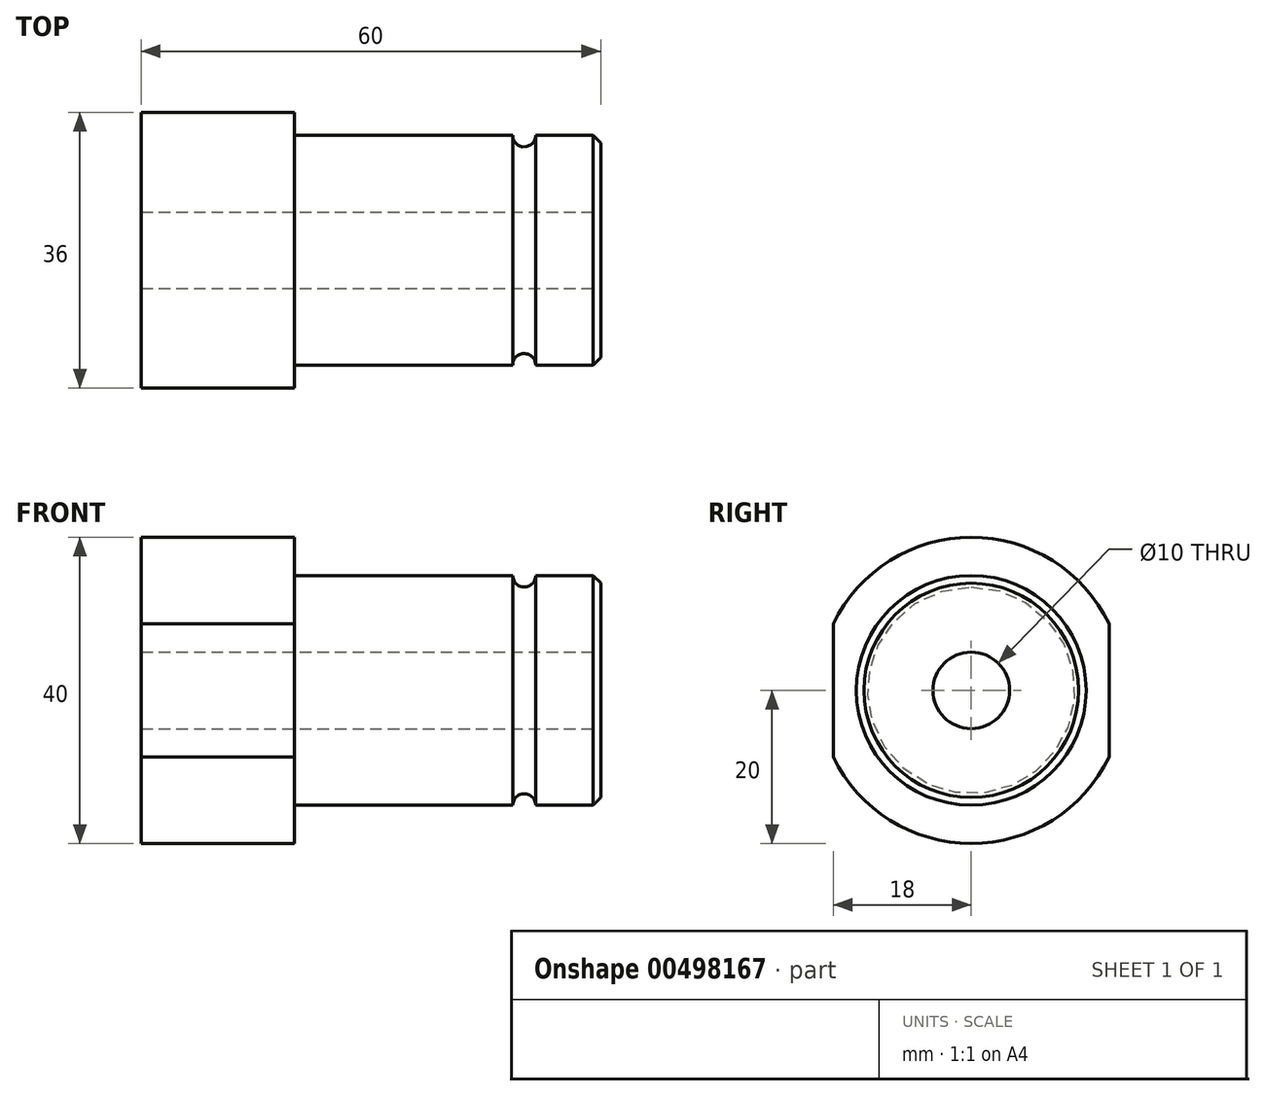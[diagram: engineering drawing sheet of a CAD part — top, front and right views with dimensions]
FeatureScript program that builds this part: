
annotation { "Feature Type Name" : "Feature", "Feature Type Description" : "" }
export const myFeature = defineFeature(function(context is Context, id is Id, definition is map)
    precondition{}
    {
        {
            var Q0;
            Q0=qCreatedBy(makeId("Front.planeOp"),FACE);
            var sketch = newSketch(context, id + "F0", { "sketchPlane" : qUnion([Q0])});
            skLineSegment(sketch, "E0", {"start": v(0, 0) * mm, "end": v(0, 20) * mm});
            skLineSegment(sketch, "E1", {"start": v(0, 20) * mm, "end": v(20, 20) * mm});
            skLineSegment(sketch, "E2", {"start": v(20, 20) * mm, "end": v(20, 15) * mm});
            skLineSegment(sketch, "E3", {"start": v(20, 15) * mm, "end": v(60, 15) * mm});
            skLineSegment(sketch, "E4", {"start": v(60, 15) * mm, "end": v(60, 0) * mm});
            skLineSegment(sketch, "E5", {"start": v(60, 0) * mm, "end": v(0, 0) * mm});
            skLineSegment(sketch, "E6", {"start": v(-6.51, 0) * mm, "end": v(42.86, 0) * mm, "construction": true});
            skCircle(sketch, "E7", {"center": v(50, 15) * mm, "radius": 1.5 * mm});
            skSolve(sketch);
        }
        {
            var Q0;
            Q0=makeQuery(id+"F0.imprint","IMPRINT",FACE,{"disambiguationData":[TD([[makeQuery(id+"F0.imprint","IMPRINT",EDGE,{"derivedFrom":sQuery(id+"F0.wireOp",EDGE,"E0")}),-1.0]])]});
            var Q1;
            Q1=sQuery(id+"F0.wireOp",EDGE,"E6");
            revolve(context, id + "F1", {"entities" : qUnion([Q0]), "axis" : qUnion([Q1]), "revolveType" : RevolveType.FULL});
        }
        {
            var Q0;
            Q0=makeQuery(id+"F1.opRevolve","SWEPT_EDGE",EDGE,{"disambiguationData":[OSD([sQuery(id+"F0.wireOp",EDGE,"E3"),sQuery(id+"F0.wireOp",EDGE,"E4")])]});
            chamfer(context, id + "F2", {"entities" : qUnion([Q0]), "width" : 1 * mm, "tangentPropagation" : true});
        }
        {
            var Q0;
            Q0=makeQuery(id+"F1.opRevolve","SWEPT_FACE",FACE,{"disambiguationData":[OSD([sQuery(id+"F0.wireOp",EDGE,"E4")])]});
            var sketch = newSketch(context, id + "F3", { "sketchPlane" : qUnion([Q0])});
            skCircle(sketch, "E8", {"center": v(0, 0) * mm, "radius": 5 * mm});
            skSolve(sketch);
        }
        {
            var Q0;
            Q0 = qSketchRegion(id + "F3", true);
            extrude(context, id + "F4", {"entities" : qUnion([Q0]), "operationType" : NewBodyOperationType.REMOVE, "endBound" : BoundingType.THROUGH_ALL, "oppositeDirection" : true, "depth" : 25 * mm, "offsetDistance" : 25 * mm});
        }
        {
            var Q0;
            Q0=makeQuery(id+"F1.opRevolve","SWEPT_FACE",FACE,{"disambiguationData":[OSD([sQuery(id+"F0.wireOp",EDGE,"E0")])]});
            var sketch = newSketch(context, id + "F5", { "sketchPlane" : qUnion([Q0])});
            skLineSegment(sketch, "E9.bottom", {"start": v(18, 20) * mm, "end": v(-18, 20) * mm});
            skLineSegment(sketch, "E9.top", {"start": v(18, -20) * mm, "end": v(-18, -20) * mm});
            skLineSegment(sketch, "E9.left", {"start": v(18, 20) * mm, "end": v(18, -20) * mm});
            skLineSegment(sketch, "E9.right", {"start": v(-18, 20) * mm, "end": v(-18, -20) * mm});
            skPoint(sketch, "E9.middle", {"position": v(0, 0) * mm});
            skSolve(sketch);
        }
        {
            var Q0;
            {var subQ0=sQuery(id+"F5.wireOp",EDGE,"E9.right");var subQ1=makeQuery(id+"F1.opRevolve","SWEPT_EDGE",EDGE,{"disambiguationData":[OSD([sQuery(id+"F0.wireOp",EDGE,"E0"),sQuery(id+"F0.wireOp",EDGE,"E1")])]});var subQ2=makeQuery(id+"F5.imprint","INTERSECT",VERTEX,{"disambiguationData":[OD(0.0)],"derivedFrom":[subQ1,subQ0]});Q0=makeQuery(id+"F5.imprint","IMPRINT",FACE,{"disambiguationData":[TD([[makeQuery(id+"F5.imprint","IMPRINT",EDGE,{"disambiguationData":[TD([[subQ2,-1.0]])],"derivedFrom":subQ0}),-1.0]])]});}
            var Q1;
            {var subQ0=sQuery(id+"F5.wireOp",EDGE,"E9.left");var subQ1=makeQuery(id+"F1.opRevolve","SWEPT_EDGE",EDGE,{"disambiguationData":[OSD([sQuery(id+"F0.wireOp",EDGE,"E0"),sQuery(id+"F0.wireOp",EDGE,"E1")])]});var subQ2=makeQuery(id+"F5.imprint","INTERSECT",VERTEX,{"disambiguationData":[OD(0.0)],"derivedFrom":[subQ1,subQ0]});Q1=makeQuery(id+"F5.imprint","IMPRINT",FACE,{"disambiguationData":[TD([[makeQuery(id+"F5.imprint","IMPRINT",EDGE,{"disambiguationData":[TD([[subQ2,-1.0]])],"derivedFrom":subQ0}),1.0]])]});}
            var Q2;
            Q2=makeQuery(id+"F1.opRevolve","SWEPT_FACE",FACE,{"disambiguationData":[OSD([sQuery(id+"F0.wireOp",EDGE,"E2")])]});
            extrude(context, id + "F6", {"entities" : qUnion([Q0, Q1]), "operationType" : NewBodyOperationType.REMOVE, "endBound" : BoundingType.UP_TO_SURFACE, "oppositeDirection" : true, "depth" : 25 * mm, "endBoundEntityFace" : qUnion([Q2]), "offsetDistance" : 25 * mm});
        }
    });
